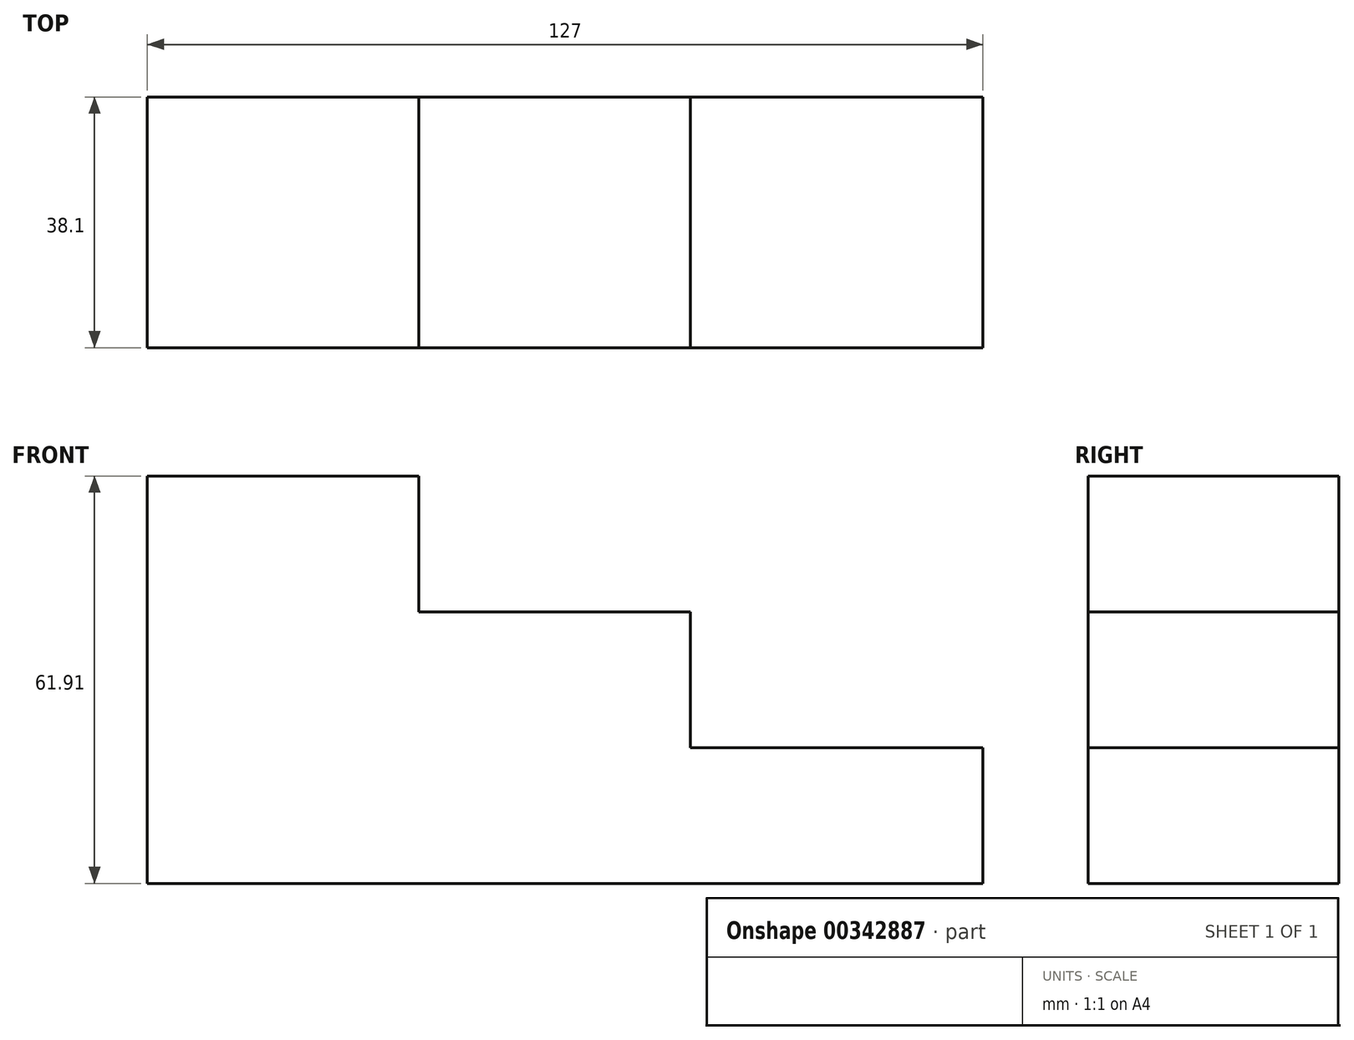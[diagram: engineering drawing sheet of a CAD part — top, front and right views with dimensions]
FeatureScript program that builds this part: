
annotation { "Feature Type Name" : "Feature", "Feature Type Description" : "" }
export const myFeature = defineFeature(function(context is Context, id is Id, definition is map)
    precondition{}
    {
        {
            var Q0;
            Q0=qCreatedBy(makeId("Front.planeOp"),FACE);
            var sketch = newSketch(context, id + "F0", { "sketchPlane" : qUnion([Q0])});
            skLineSegment(sketch, "E0.bottom", {"start": v(-84.49, -36.54) * mm, "end": v(42.51, -36.54) * mm});
            skLineSegment(sketch, "E0.top", {"start": v(-84.49, -15.9) * mm, "end": v(42.51, -15.9) * mm});
            skLineSegment(sketch, "E0.left", {"start": v(-84.49, -36.54) * mm, "end": v(-84.49, -15.9) * mm});
            skLineSegment(sketch, "E0.right", {"start": v(42.51, -36.54) * mm, "end": v(42.51, -15.9) * mm});
            skLineSegment(sketch, "E1.bottom", {"start": v(-84.49, -15.9) * mm, "end": v(-1.94, -15.9) * mm});
            skLineSegment(sketch, "E1.top", {"start": v(-84.49, 4.73) * mm, "end": v(-1.94, 4.73) * mm});
            skLineSegment(sketch, "E1.left", {"start": v(-84.49, -15.9) * mm, "end": v(-84.49, 4.73) * mm});
            skLineSegment(sketch, "E1.right", {"start": v(-1.94, -15.9) * mm, "end": v(-1.94, 4.73) * mm});
            skLineSegment(sketch, "E2.bottom", {"start": v(-84.49, 4.73) * mm, "end": v(-43.21, 4.73) * mm});
            skLineSegment(sketch, "E2.top", {"start": v(-84.49, 25.37) * mm, "end": v(-43.21, 25.37) * mm});
            skLineSegment(sketch, "E2.left", {"start": v(-84.49, 4.73) * mm, "end": v(-84.49, 25.37) * mm});
            skLineSegment(sketch, "E2.right", {"start": v(-43.21, 4.73) * mm, "end": v(-43.21, 25.37) * mm});
            skSolve(sketch);
        }
        {
            var Q0;
            Q0 = qSketchRegion(id + "F0", true);
            extrude(context, id + "F1", {"entities" : qUnion([Q0]), "depth" : 38.1 * mm});
        }
    });
